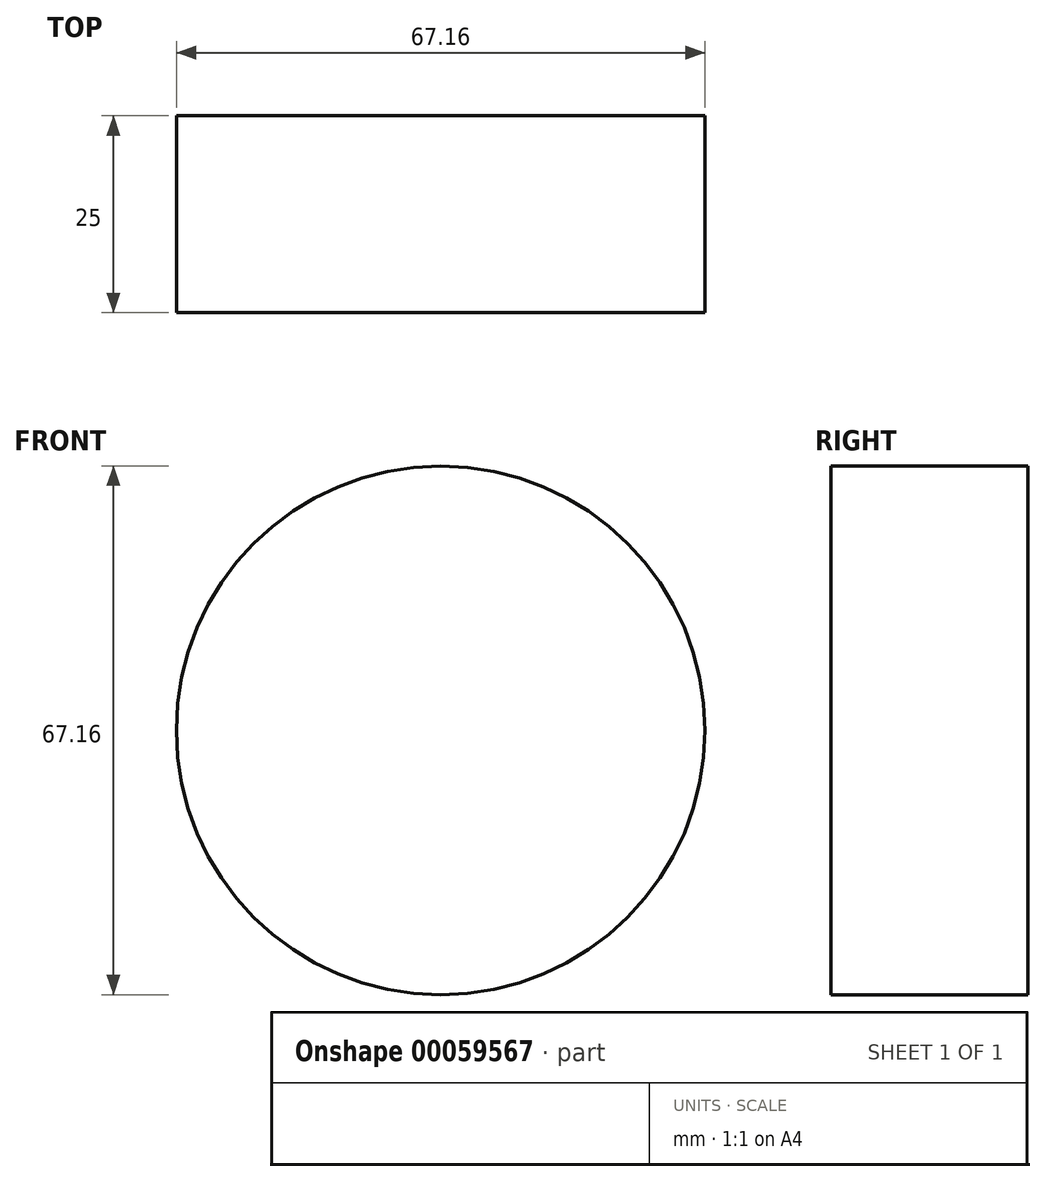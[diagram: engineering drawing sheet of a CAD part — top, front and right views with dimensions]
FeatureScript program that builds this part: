
annotation { "Feature Type Name" : "Feature", "Feature Type Description" : "" }
export const myFeature = defineFeature(function(context is Context, id is Id, definition is map)
    precondition{}
    {
        {
            var Q0;
            Q0=qCreatedBy(makeId("Front.planeOp"),FACE);
            var sketch = newSketch(context, id + "F0", { "sketchPlane" : qUnion([Q0])});
            skCircle(sketch, "E0", {"center": v(0, 0) * mm, "radius": 33.58 * mm});
            skSolve(sketch);
        }
        {
            var Q0;
            Q0=makeQuery(id+"F0.imprint","IMPRINT",FACE,{"disambiguationData":[TD([[makeQuery(id+"F0.imprint","IMPRINT",EDGE,{"derivedFrom":sQuery(id+"F0.wireOp",EDGE,"E0")}),1.0]])]});
            extrude(context, id + "F1", {"entities" : qUnion([Q0]), "depth" : 25 * mm});
        }
    });
